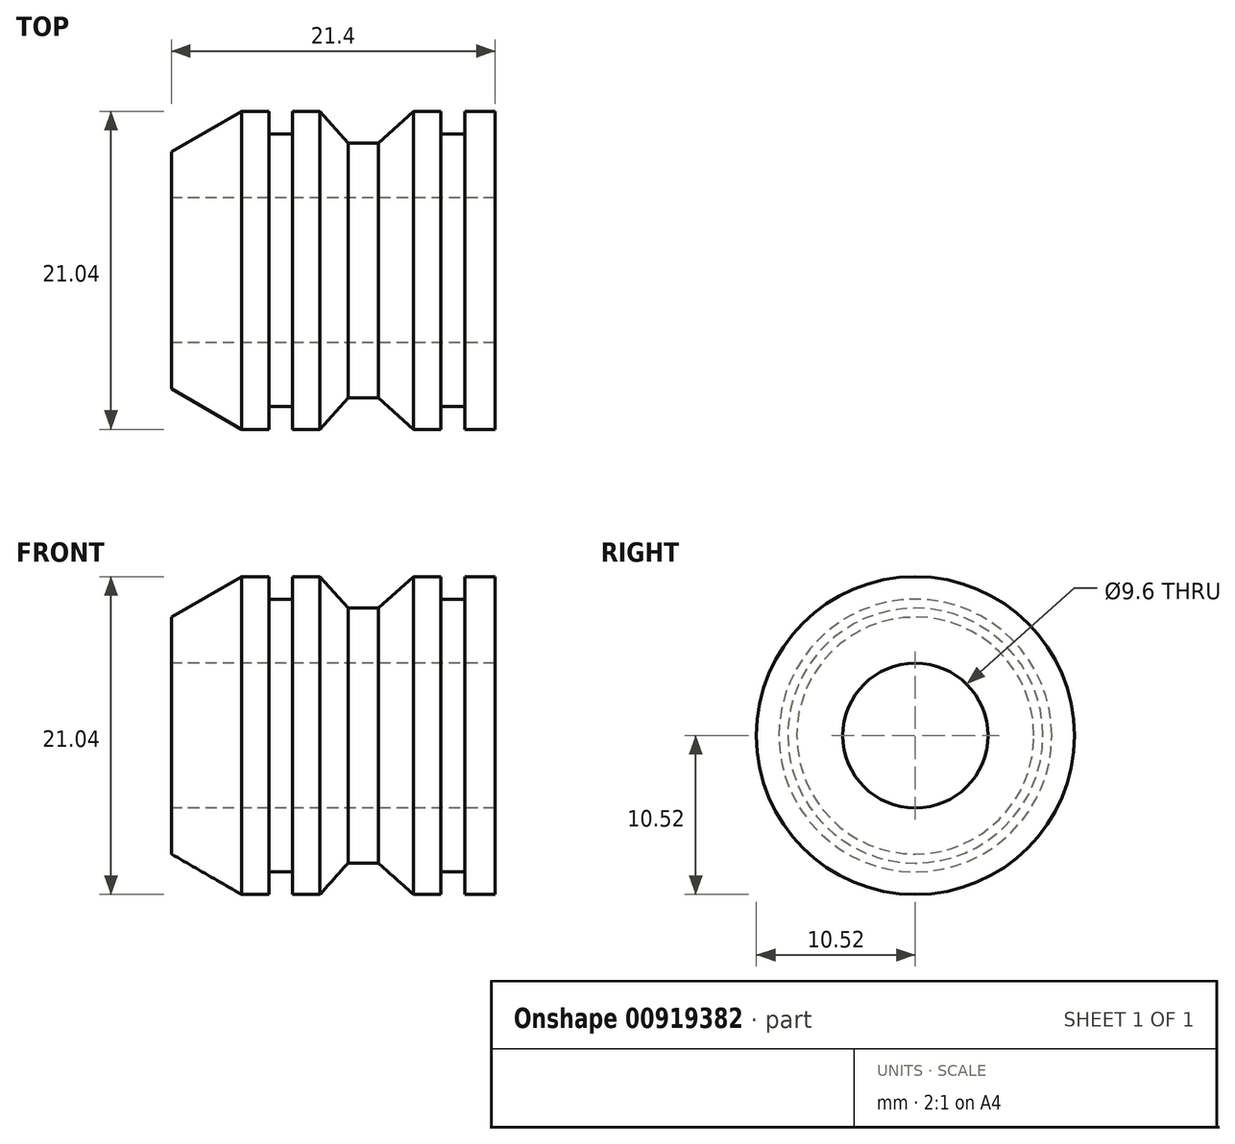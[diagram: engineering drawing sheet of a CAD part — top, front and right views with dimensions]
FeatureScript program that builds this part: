
annotation { "Feature Type Name" : "Feature", "Feature Type Description" : "" }
export const myFeature = defineFeature(function(context is Context, id is Id, definition is map)
    precondition{}
    {
        {
            var Q0;
            Q0=qCreatedBy(makeId("Front.planeOp"),FACE);
            var sketch = newSketch(context, id + "F0", { "sketchPlane" : qUnion([Q0])});
            skLineSegment(sketch, "E0", {"start": v(0, 17.2) * mm, "end": v(0, 0) * mm});
            skLineSegment(sketch, "E1", {"start": v(4.64, 19.88) * mm, "end": v(6.44, 19.88) * mm});
            skLineSegment(sketch, "E2", {"start": v(0, 17.2) * mm, "end": v(4.64, 19.88) * mm});
            skLineSegment(sketch, "E3", {"start": v(6.44, 19.88) * mm, "end": v(6.44, 18.38) * mm});
            skLineSegment(sketch, "E4", {"start": v(6.44, 18.38) * mm, "end": v(8.02, 18.38) * mm});
            skLineSegment(sketch, "E5", {"start": v(8.02, 18.38) * mm, "end": v(8.02, 19.88) * mm});
            skLineSegment(sketch, "E6", {"start": v(8.02, 19.88) * mm, "end": v(9.82, 19.88) * mm});
            skLineSegment(sketch, "E7", {"start": v(11.68, 17.8) * mm, "end": v(9.82, 19.88) * mm});
            skLineSegment(sketch, "E8", {"start": v(11.68, 17.8) * mm, "end": v(13.68, 17.8) * mm});
            skLineSegment(sketch, "E9", {"start": v(13.68, 17.8) * mm, "end": v(16.02, 19.88) * mm});
            skLineSegment(sketch, "E10", {"start": v(16.02, 19.88) * mm, "end": v(17.82, 19.88) * mm});
            skLineSegment(sketch, "E11", {"start": v(17.82, 19.88) * mm, "end": v(17.82, 18.38) * mm});
            skLineSegment(sketch, "E12", {"start": v(17.82, 18.38) * mm, "end": v(19.4, 18.38) * mm});
            skLineSegment(sketch, "E13", {"start": v(19.4, 18.38) * mm, "end": v(19.4, 19.88) * mm});
            skLineSegment(sketch, "E14", {"start": v(19.4, 19.88) * mm, "end": v(21.4, 19.88) * mm});
            skLineSegment(sketch, "E15", {"start": v(21.4, 19.88) * mm, "end": v(21.4, -1.92) * mm});
            skLineSegment(sketch, "E16.MirrorCS", {"start": v(11.68, 0.16) * mm, "end": v(13.68, 0.16) * mm});
            skLineSegment(sketch, "E17.MirrorCS", {"start": v(11.68, 0.16) * mm, "end": v(9.82, -1.92) * mm});
            skLineSegment(sketch, "E18.MirrorCS", {"start": v(19.4, -1.92) * mm, "end": v(21.4, -1.92) * mm});
            skLineSegment(sketch, "E19.MirrorCS", {"start": v(6.44, -0.42) * mm, "end": v(8.02, -0.42) * mm});
            skLineSegment(sketch, "E20.MirrorCS", {"start": v(17.82, -0.42) * mm, "end": v(19.4, -0.42) * mm});
            skLineSegment(sketch, "E21.MirrorCS", {"start": v(16.02, -1.92) * mm, "end": v(17.82, -1.92) * mm});
            skLineSegment(sketch, "E22.MirrorCS", {"start": v(8.02, -1.92) * mm, "end": v(9.82, -1.92) * mm});
            skLineSegment(sketch, "E23.MirrorCS", {"start": v(19.4, -0.42) * mm, "end": v(19.4, -1.92) * mm});
            skLineSegment(sketch, "E24.MirrorCS", {"start": v(4.64, -1.92) * mm, "end": v(6.44, -1.92) * mm});
            skLineSegment(sketch, "E25.MirrorCS", {"start": v(6.44, -1.92) * mm, "end": v(6.44, -0.42) * mm});
            skLineSegment(sketch, "E26.MirrorCS", {"start": v(8.02, -0.42) * mm, "end": v(8.02, -1.92) * mm});
            skLineSegment(sketch, "E27.MirrorCS", {"start": v(17.82, -1.92) * mm, "end": v(17.82, -0.42) * mm});
            skLineSegment(sketch, "E28.MirrorCS", {"start": v(13.68, 0.16) * mm, "end": v(16.02, -1.92) * mm});
            skLineSegment(sketch, "E29.MirrorCS", {"start": v(0, 0.76) * mm, "end": v(4.64, -1.92) * mm});
            skLineSegment(sketch, "E30", {"start": v(0, 17.2) * mm, "end": v(0, 8.6) * mm});
            skLineSegment(sketch, "E31", {"start": v(21.4, 13.4) * mm, "end": v(0, 13.4) * mm, "construction": true});
            skLineSegment(sketch, "E32", {"start": v(0, 3.8) * mm, "end": v(21.4, 3.8) * mm, "construction": true});
            skPoint(sketch, "E33.MirrorCS.start.orphan", {"position": v(0, 0.76) * mm});
            skLineSegment(sketch, "E34", {"start": v(0, 8.6) * mm, "end": v(21.4, 8.6) * mm});
            skSolve(sketch);
        }
        {
            var Q0;
            Q0=makeQuery(id+"F0.imprint","IMPRINT",FACE,{"disambiguationData":[TD([[makeQuery(id+"F0.imprint","IMPRINT",EDGE,{"derivedFrom":sQuery(id+"F0.wireOp",EDGE,"E16.MirrorCS")}),1.0]])]});
            var Q1;
            Q1=sQuery(id+"F0.wireOp",EDGE,"E34");
            revolve(context, id + "F1", {"surfaceOperationType" : NewSurfaceOperationType.NEW, "entities" : qUnion([Q0]), "axis" : qUnion([Q1]), "revolveType" : RevolveType.ONE_DIRECTION, "oppositeDirection" : true, "angle" : 360 * degree});
        }
        {
            var Q0;
            Q0=makeQuery(id+"F1.opRevolve","SWEPT_FACE",FACE,{"disambiguationData":[OSD([sQuery(id+"F0.wireOp",EDGE,"E0")])]});
            var sketch = newSketch(context, id + "F2", { "sketchPlane" : qUnion([Q0])});
            skCircle(sketch, "E35", {"center": v(0, 8.6) * mm, "radius": 4.8 * mm});
            skSolve(sketch);
        }
        {
            var Q0;
            Q0=makeQuery(id+"F2.imprint","IMPRINT",FACE,{"disambiguationData":[TD([[makeQuery(id+"F2.imprint","IMPRINT",EDGE,{"derivedFrom":sQuery(id+"F2.wireOp",EDGE,"E35")}),1.0]])]});
            extrude(context, id + "F3", {"entities" : qUnion([Q0]), "operationType" : NewBodyOperationType.REMOVE, "oppositeDirection" : true, "depth" : 25 * mm, "offsetDistance" : 25 * mm});
        }
    });
